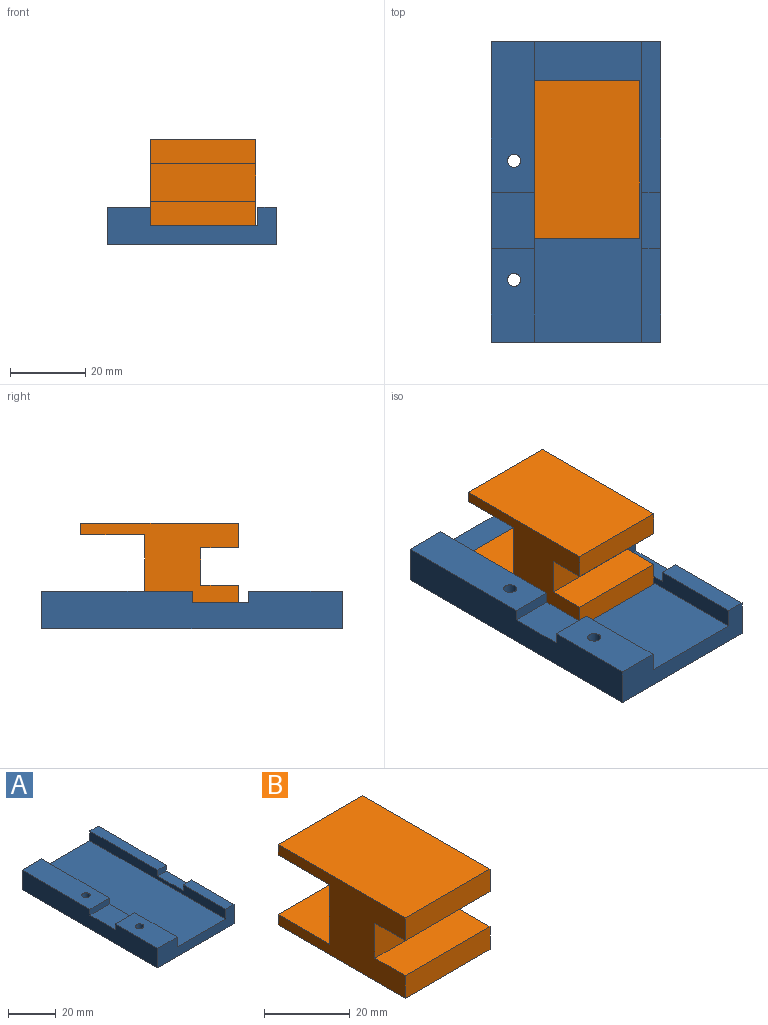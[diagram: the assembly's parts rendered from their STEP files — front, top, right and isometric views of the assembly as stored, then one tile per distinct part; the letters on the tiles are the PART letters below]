
ASSEMBLY  parts=2 mates=2
PART A: 20 faces, bbox 45x80x10 mm
  f0: plane 40.05x5mm, normal (0,0,1), area 200.3mm2, adj f4,f8,f10,f16
  f1: plane 40.05x11.5mm, normal (0,0,1), area 451mm2, adj f2,f3,f10,f11,f17
  f2: plane 80x10mm, normal (-1,0,0), area 755mm2, adj f1,f6,f7,f9,f10,f17,f18,f19
  f3: plane 80x5mm, normal (1,0,0), area 355mm2, adj f1,f6,f9,f10,f13,f17,f18,f19
  f4: plane 80x5mm, normal (-1,0,0), area 355mm2, adj f0,f5,f6,f10,f13,f14,f15,f16
  f5: plane 24.95x5mm, normal (0,0,1), area 124.7mm2, adj f4,f6,f8,f15
  f6: plane 45x10mm, normal (0,-1,0), area 307.5mm2, adj f2,f3,f4,f5,f7,f8,f9,f13
  f7: plane 80x45mm, normal (0,0,-1), area 3580.8mm2, adj f2,f6,f8,f10,f11,f12
  f8: plane 80x10mm, normal (1,0,0), area 755mm2, adj f0,f5,f6,f7,f10,f14,f15,f16
  f9: plane 24.95x11.5mm, normal (0,0,1), area 277.3mm2, adj f2,f3,f6,f12,f18
  f10: plane 45x10mm, normal (0,1,0), area 307.5mm2, adj f0,f1,f2,f3,f4,f7,f8,f13
  f11: cylinder r=1.75mm len=10mm, axis (0,0,1), area 110mm2, adj f1,f7
  f12: cylinder r=1.75mm len=10mm, axis (0,0,1), area 110mm2, adj f7,f9
  f13: plane 80x28.5mm, normal (0,0,1), area 2280mm2, adj f3,f4,f6,f10
  f14: plane 15x5mm, normal (0,0,1), area 75mm2, adj f4,f8,f15,f16
  f15: plane 5x3mm, normal (0,1,0), area 15mm2, adj f4,f5,f8,f14
  f16: plane 5x3mm, normal (0,-1,0), area 15mm2, adj f0,f4,f8,f14
  f17: plane 11.5x3mm, normal (0,-1,0), area 34.5mm2, adj f1,f2,f3,f19
  f18: plane 11.5x3mm, normal (0,1,0), area 34.5mm2, adj f2,f3,f9,f19
  f19: plane 15x11.5mm, normal (0,0,1), area 172.5mm2, adj f2,f3,f17,f18
PART B: 14 faces, bbox 28x42x23 mm
  f0: plane 28x3mm, normal (0,1,0), area 84mm2, adj f1,f4,f5,f12
  f1: plane 42x23mm, normal (-1,0,0), area 577mm2, adj f0,f2,f3,f5,f6,f7,f8,f9
  f2: plane 28x6.5mm, normal (0,-1,0), area 182mm2, adj f1,f4,f5,f8
  f3: plane 42x28mm, normal (0,0,-1), area 1176mm2, adj f1,f4,f6,f7
  f4: plane 42x23mm, normal (1,0,0), area 577mm2, adj f0,f2,f3,f5,f6,f7,f8,f9
  f5: plane 42x28mm, normal (0,0,1), area 1176mm2, adj f0,f1,f2,f4
  f6: plane 28x6.5mm, normal (0,-1,0), area 182mm2, adj f1,f3,f4,f9
  f7: plane 28x3mm, normal (0,1,0), area 84mm2, adj f1,f3,f4,f11
  f8: plane 28x10mm, normal (0,0,-1), area 280mm2, adj f1,f2,f4,f10
  f9: plane 28x10mm, normal (0,0,1), area 280mm2, adj f1,f4,f6,f10
  f10: plane 28x10mm, normal (0,-1,0), area 280mm2, adj f1,f4,f8,f9
  f11: plane 28x17mm, normal (0,0,1), area 476mm2, adj f1,f4,f7,f13
  f12: plane 28x17mm, normal (0,0,-1), area 476mm2, adj f0,f1,f4,f13
  f13: plane 28x17mm, normal (0,1,0), area 476mm2, adj f1,f4,f11,f12
PLACE A t=(-2.53,32.15,-3.17)mm
PLACE B t=(10.56,21.79,1.83)mm
MATE planar B.f3 <-> A.f13  axis (0,0,-1) through (24.56,0.79,1.83)mm
MATE planar B.f1 <-> A.f3  axis (-1,0,0) through (10.56,-2.69,13.33)mm
